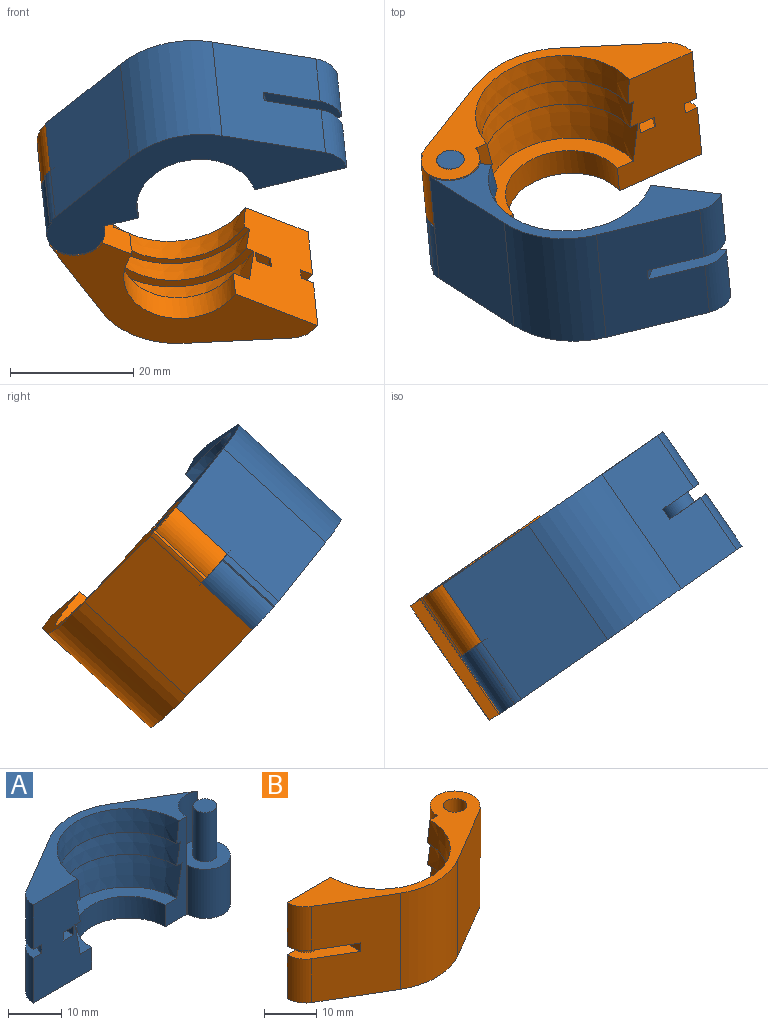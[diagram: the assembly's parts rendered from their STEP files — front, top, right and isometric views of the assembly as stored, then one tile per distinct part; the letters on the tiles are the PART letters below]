
ASSEMBLY  parts=2 mates=1
PART A: 28 faces, bbox 50.4x20.1x22.6 mm
  f0: plane 9.8x9.76mm, normal (0,0,1), area 58.1mm2, adj f16,f17,f19,f25,f26,f27
  f1: plane 22.6x15.53mm, normal (0,-1,0), area 277.8mm2, adj f3,f5,f8,f9,f10,f11,f12,f13
  f2: plane 22.6x15.07mm, normal (-0.51,0.86,0), area 376.1mm2, adj f3,f5,f7,f14,f15,f21,f23,f24
  f3: cylinder r=5mm len=10.3mm, axis (0,0,-1), area 53.5mm2, adj f1,f2,f15,f23
  f4: plane 22.6x5.54mm, normal (0,-1,0), area 62.2mm2, adj f5,f8,f9,f10,f11,f12,f13,f15
  f5: plane 50.37x20.1mm, normal (0,0,-1), area 390.4mm2, adj f1,f2,f4,f6,f7,f14,f16,f20
  f6: plane 22.6x14.88mm, normal (0.51,0.86,0), area 390.4mm2, adj f5,f7,f15,f16,f17
  f7: cylinder r=15.3mm len=22.6mm, axis (0,0,-1), area 368mm2, adj f2,f5,f6,f15
  f8: cone r=19.01mm half-angle=7.4deg, axis (0,0,1), area 207.8mm2, adj f1,f4,f9,f15
  f9: plane 27.61x13.81mm, normal (0,0,-1), area 42mm2, adj f1,f4,f8,f10
  f10: cone r=13.81mm half-angle=11.1deg, axis (0,0,1), area 217.3mm2, adj f1,f4,f9,f11
  f11: plane 28.5x14.25mm, normal (0,0,-1), area 61.6mm2, adj f1,f4,f10,f12
  f12: cone r=14.25mm half-angle=10.9deg, axis (0,0,1), area 324.6mm2, adj f1,f4,f11,f13
  f13: plane 25.61x12.88mm, normal (0,0,1), area 107.3mm2, adj f1,f4,f12,f20
  f14: cylinder r=5mm len=10.3mm, axis (0,0,-1), area 53.5mm2, adj f1,f2,f5,f24
  f15: plane 47.95x15.3mm, normal (0,0,1), area 182.4mm2, adj f1,f2,f3,f4,f6,f7,f8,f17
  f16: cylinder r=5mm len=11.3mm, axis (0,0,-1), area 16.3mm2, adj f0,f5,f6,f27
  f17: cylinder r=5mm len=11.3mm, axis (0,0,1), area 116.2mm2, adj f0,f4,f6,f15
  f18: plane 4.5x4.5mm, normal (0,0,1), area 15.9mm2, adj f19
  f19: cylinder r=2.25mm len=11.3mm, axis (0,0,-1), area 159.7mm2, adj f0,f18
  f20: cylinder r=9.77mm len=19.55mm, axis (0,0,1), area 153.5mm2, adj f1,f4,f5,f13
  f21: plane 9.2x2mm, normal (-1,0,0), area 18.4mm2, adj f1,f2,f23,f24
  f22: cylinder r=2.82mm len=5.64mm, axis (0,0,-1), area 17.7mm2, adj f1,f23,f24
  f23: plane 10.76x9.2mm, normal (0,0,-1), area 51.1mm2, adj f1,f2,f3,f21,f22
  f24: plane 10.76x9.2mm, normal (0,0,1), area 51.1mm2, adj f1,f2,f14,f21,f22
  f25: plane 11.3x0.3mm, normal (-0.01,-1,0), area 3.4mm2, adj f0,f4,f5,f26
  f26: cylinder r=4.73mm len=11.3mm, axis (0,0,-1), area 211.8mm2, adj f0,f5,f25,f27
  f27: cylinder r=0.15mm len=11.3mm, axis (0,0,-1), area 4.8mm2, adj f0,f5,f16,f26
PART B: 28 faces, bbox 50.4x20.1x22.6 mm
  f0: plane 9.82x9.78mm, normal (0,0,-1), area 58.6mm2, adj f1,f5,f9,f17,f18,f19,f25,f26
  f1: cylinder r=5mm len=11.3mm, axis (0,0,1), area 0mm2, adj f0,f5,f7,f25
  f2: plane 22.6x15.53mm, normal (0,1,0), area 277.8mm2, adj f3,f6,f7,f8,f11,f12,f13,f14
  f3: cylinder r=5mm len=10.3mm, axis (0,0,-1), area 53.5mm2, adj f2,f4,f7,f23
  f4: plane 22.6x15.07mm, normal (-0.51,-0.86,0), area 376.1mm2, adj f3,f6,f7,f8,f10,f22,f23,f24
  f5: plane 22.6x5.54mm, normal (0,1,0), area 62.3mm2, adj f0,f1,f6,f7,f11,f12,f13,f14
  f6: plane 47.95x15.3mm, normal (0,0,-1), area 316.3mm2, adj f2,f4,f5,f8,f9,f10,f18,f20
  f7: plane 50.39x20.12mm, normal (0,0,1), area 241mm2, adj f1,f2,f3,f4,f5,f9,f10,f16
  f8: cylinder r=5mm len=10.3mm, axis (0,0,-1), area 53.5mm2, adj f2,f4,f6,f24
  f9: plane 22.6x14.88mm, normal (0.51,-0.86,0), area 390.3mm2, adj f0,f6,f7,f10,f17,f18
  f10: cylinder r=15.3mm len=22.6mm, axis (0,0,-1), area 368mm2, adj f4,f6,f7,f9
  f11: plane 25.61x12.88mm, normal (0,0,1), area 107.3mm2, adj f2,f5,f12,f20
  f12: cone r=14.25mm half-angle=10.9deg, axis (0,0,1), area 324.6mm2, adj f2,f5,f11,f13
  f13: plane 28.5x14.25mm, normal (0,0,-1), area 61.6mm2, adj f2,f5,f12,f14
  f14: cone r=13.81mm half-angle=11.1deg, axis (0,0,1), area 217.3mm2, adj f2,f5,f13,f15
  f15: plane 27.61x13.81mm, normal (0,0,-1), area 42mm2, adj f2,f5,f14,f16
  f16: cone r=19.01mm half-angle=7.4deg, axis (0,0,1), area 207.8mm2, adj f2,f5,f7,f15
  f17: cylinder r=5mm len=11.3mm, axis (0,0,1), area 11.2mm2, adj f0,f7,f9,f27
  f18: cylinder r=5mm len=11.3mm, axis (0,0,-1), area 116.2mm2, adj f0,f5,f6,f9
  f19: cylinder r=2.25mm len=11.3mm, axis (0,0,-1), area 159.7mm2, adj f0,f7
  f20: cylinder r=9.77mm len=19.55mm, axis (0,0,1), area 153.5mm2, adj f2,f5,f6,f11
  f21: cylinder r=2.82mm len=5.64mm, axis (0,0,-1), area 17.7mm2, adj f2,f23,f24
  f22: plane 9.2x2mm, normal (-1,0,0), area 18.4mm2, adj f2,f4,f23,f24
  f23: plane 10.76x9.2mm, normal (0,0,-1), area 51.1mm2, adj f2,f3,f4,f21,f22
  f24: plane 10.76x9.2mm, normal (0,0,1), area 51.1mm2, adj f2,f4,f8,f21,f22
  f25: plane 11.3x0.23mm, normal (0,1,0), area 2.6mm2, adj f0,f1,f7,f26
  f26: cylinder r=4.77mm len=11.3mm, axis (0,0,1), area 215.2mm2, adj f0,f7,f25,f27
  f27: plane 11.3x0.37mm, normal (0.99,-0.1,0), area 4.2mm2, adj f0,f7,f17,f26
PLACE A rot(axis=(-0.08,0.4,0.91),168.1deg) t=(-95.17,43.09,-26.31)mm
PLACE B rot(axis=(-0.08,-0.41,-0.91),150.8deg) t=(-97.27,53.44,-37.72)mm
MATE revolute A.f16 <-> B.f18  axis (0.07,-0.74,-0.67) through (-111.4,9.82,-63.84)mm
